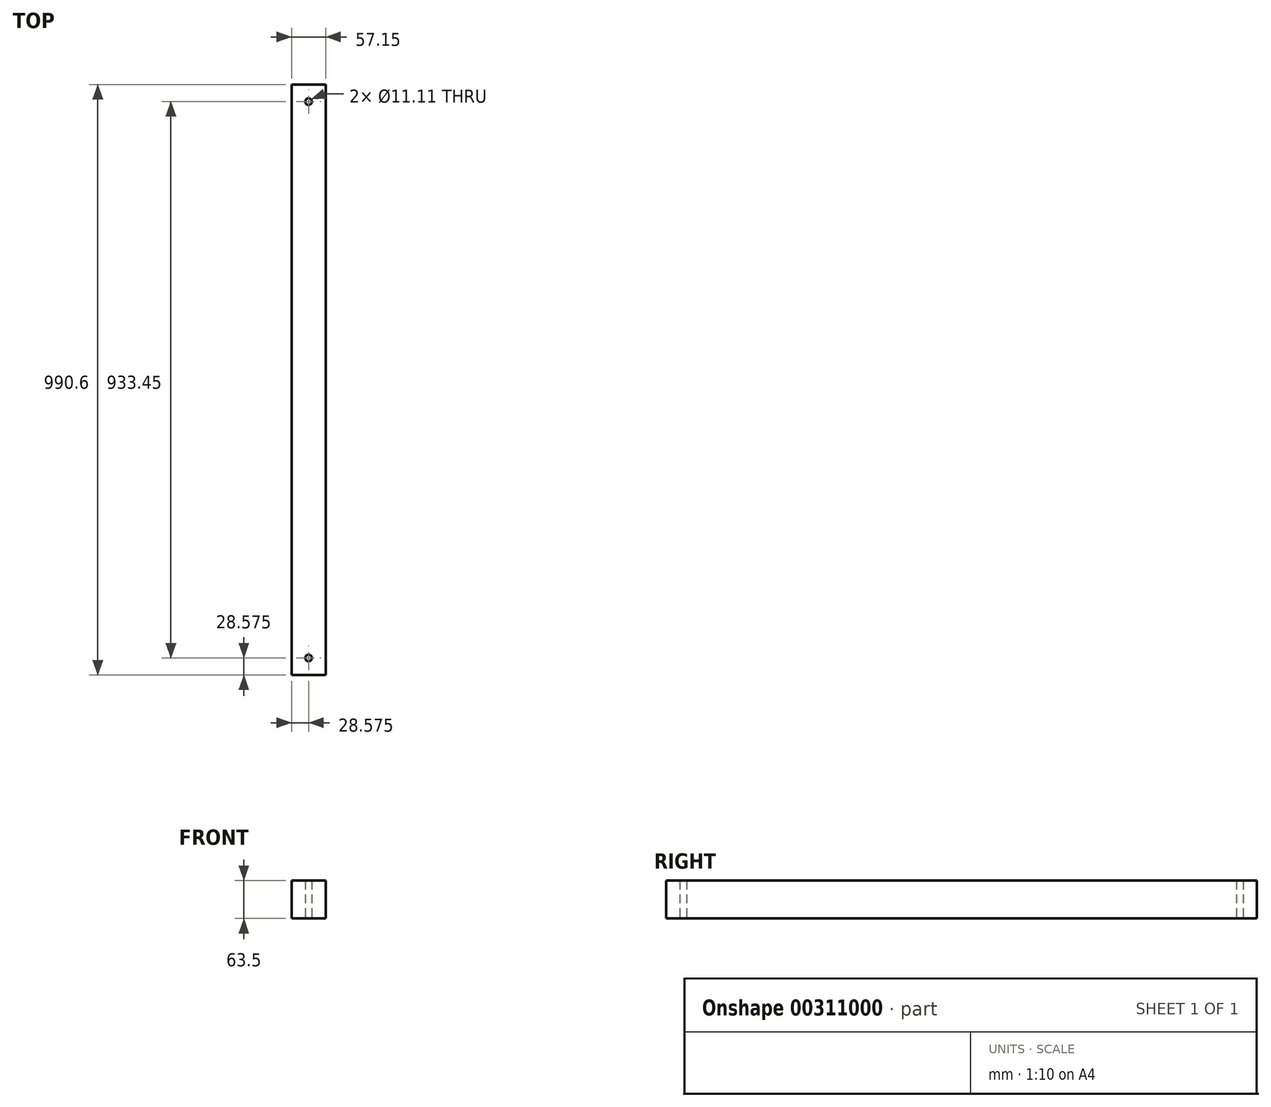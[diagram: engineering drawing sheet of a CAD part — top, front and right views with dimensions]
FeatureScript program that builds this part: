
annotation { "Feature Type Name" : "Feature", "Feature Type Description" : "" }
export const myFeature = defineFeature(function(context is Context, id is Id, definition is map)
    precondition{}
    {
        {
            var Q0;
            Q0=qCreatedBy(makeId("Front.planeOp"),FACE);
            var sketch = newSketch(context, id + "F0", { "sketchPlane" : qUnion([Q0])});
            skLineSegment(sketch, "E0.bottom", {"start": v(0, 0) * mm, "end": v(57.15, 0) * mm});
            skLineSegment(sketch, "E0.top", {"start": v(0, -63.5) * mm, "end": v(57.15, -63.5) * mm});
            skLineSegment(sketch, "E0.left", {"start": v(0, 0) * mm, "end": v(0, -63.5) * mm});
            skLineSegment(sketch, "E0.right", {"start": v(57.15, 0) * mm, "end": v(57.15, -63.5) * mm});
            skSolve(sketch);
        }
        {
            var Q0;
            Q0=makeQuery(id+"F0.imprint","IMPRINT",FACE,{"disambiguationData":[TD([[makeQuery(id+"F0.imprint","IMPRINT",EDGE,{"derivedFrom":sQuery(id+"F0.wireOp",EDGE,"E0.bottom")}),-1.0]])]});
            extrude(context, id + "F1", {"entities" : qUnion([Q0]), "oppositeDirection" : true, "depth" : 990.6 * mm});
        }
        {
            var Q0;
            Q0=makeQuery(id+"F1.opExtrude","SWEPT_FACE",FACE,{"disambiguationData":[OSD([sQuery(id+"F0.wireOp",EDGE,"E0.bottom")])]});
            var sketch = newSketch(context, id + "F2", { "sketchPlane" : qUnion([Q0])});
            skLineSegment(sketch, "E1", {"start": v(28.58, 0) * mm, "end": v(28.57, 990.6) * mm, "construction": true});
            skPoint(sketch, "E2", {"position": v(28.58, 28.58) * mm});
            skPoint(sketch, "E3", {"position": v(28.57, 962.03) * mm});
            skSolve(sketch);
        }
        {
            var Q0;
            Q0=sQuery(id+"F2.wireOp",VERTEX,"E3");
            var Q1;
            Q1=sQuery(id+"F2.wireOp",VERTEX,"E2");
            var Q2;
            Q2=makeQuery(id+"F1.opExtrude","SWEPT_BODY",BODY,{"disambiguationData":[OSD([sQuery(id+"F0.wireOp",EDGE,"E0.bottom"),sQuery(id+"F0.wireOp",EDGE,"E0.top"),sQuery(id+"F0.wireOp",EDGE,"E0.left"),sQuery(id+"F0.wireOp",EDGE,"E0.right")])]});
            hole(context, id + "F3", {"style" : HoleStyle.SIMPLE, "endStyle" : HoleEndStyle.THROUGH, "holeDiameter" : 11.1 * mm, "tappedDepth" : 12.7 * mm, "tapClearance" : 3, "locations" : qUnion([Q0, Q1]), "scope" : qUnion([Q2])});
        }
    });
